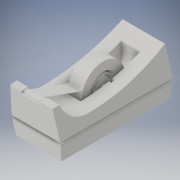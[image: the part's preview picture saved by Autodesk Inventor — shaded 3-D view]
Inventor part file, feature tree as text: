
AUTODESK INVENTOR PART (.ipt)
format: ipt  version: 2017 (Build 210142000, 142)  size: 634,368 bytes
history: native  units: in
note: dims shown in document units (in); Inventor stores cm internally (conversion verified against a paired STEP export)
features: sketch x11, extrude x10, other x4, mirror x1, fillet x1
ambient origin geometry x8: Origin, YZ Plane, XZ Plane, XY Plane, X Axis, Y Axis, Z Axis, Center Point
bodies: Solid1 (feature_tree), Solid2 (feature_tree)
feature tree (27):
  extrude  "side view"  Depth=0.0063in
  extrude  "front view"  Depth=0.1374in
  extrude  "tape gap"  Depth=0.011in
  extrude  "tape holder rack"  Depth=0.1372in
  mirror  "mirror tape holder rack"
  other  "axle for tape workplane"
  other  "axle for tape"
  extrude  "tape holder"  Depth=0.353in
  sketch  "Sketch8"  dims[d11=0.0889in d12=0.2191in d13=0.0in]
  other  "tape ring"
  other  "tape"
  extrude  "inner of cutter"  Depth=0.2191in TaperAngle=0.0deg
  extrude  "middle of cutter"  Depth=0.1382in
  extrude  "outer of cutter"  Depth=0.5774in
  extrude  "cutting teeth"  Depth=0.0672in
  extrude  "tap to cutter"  Depth=0.1409in
  fillet  "smooth edges"  Radius=0.0698in
  sketch  "Sketch1"  dims[d1=0.0723in d2=0.0063in]
  sketch  "Sketch2"  dims[d3=0.0107in d4=0.1374in]
  sketch  "Sketch3"  dims[d5=0.1392in d6=0.011in]
  sketch  "Sketch4"  dims[d7=0.4882in d8=0.1372in]
  sketch  "Sketch5"  dims[d9=0.032in d10=0.353in]
  sketch  "Sketch10"  dims[d14=0.4882in d15=0.1382in]
  sketch  "Sketch11"  dims[d17=0.5774in d18=0.5774in]
  sketch  "Sketch12"  dims[d19=0.2191in d20=0.0in d21=0.0672in]
  sketch  "Sketch13"  dims[d22=0.2719in d23=0.1409in d24=0.0698in]
  sketch  "Sketch14"  dims[d25=0.0128in d28=0.0113in d30=0.0845in d31=0.0in d32=0.1267in d33=0.0105in d34=0.0063in d35=0.006in d36=0.018in d38=0.0234in d39=0.0388in d40=0.0125in d41=0.0in d42=0.0117in d44=0.1071in d45=0.008in d48=0.009in d49=90.0deg d53=0.0308in d54=0.0098in d55=0.052in d57=0.0798in d58=0.0745in d59=0.0405in d61=0.0126in d62=0.0126in d67=0.0387in d68=0.0618in d69=0.0in d70=0.043in d71=0.043in d73=0.0298in d74=0.0112in d75=0.0028in d76=0.0028in d77=0.0366in d81=90.0deg d82=90.0deg d87=0.0295in d88=0.011in d89=0.001in d90=0.0149in d91=0.0034in d93=0.0047in d94=0.0145in d96=0.0052in d97=0.0035in d98=0.0054in d99=0.0027in d100=0.0048in d101=0.0048in d102=0.0023in d103=0.0371in d104=0.0in d107=0.0238in d108=0.0778in d109=0.0in d110=0.003in d111=0.0053in d112=0.0858in d113=0.0in d114=0.0858in d115=0.0034in d117=0.0018in d154=0.0858in d155=0.0in d156=0.028in d157=0.0003in d159=0.0062in d160=0.0003in d161=0.0618in d162=0.0in d163=0.0618in d164=0.002in d165=0.011in d166=0.011in]
